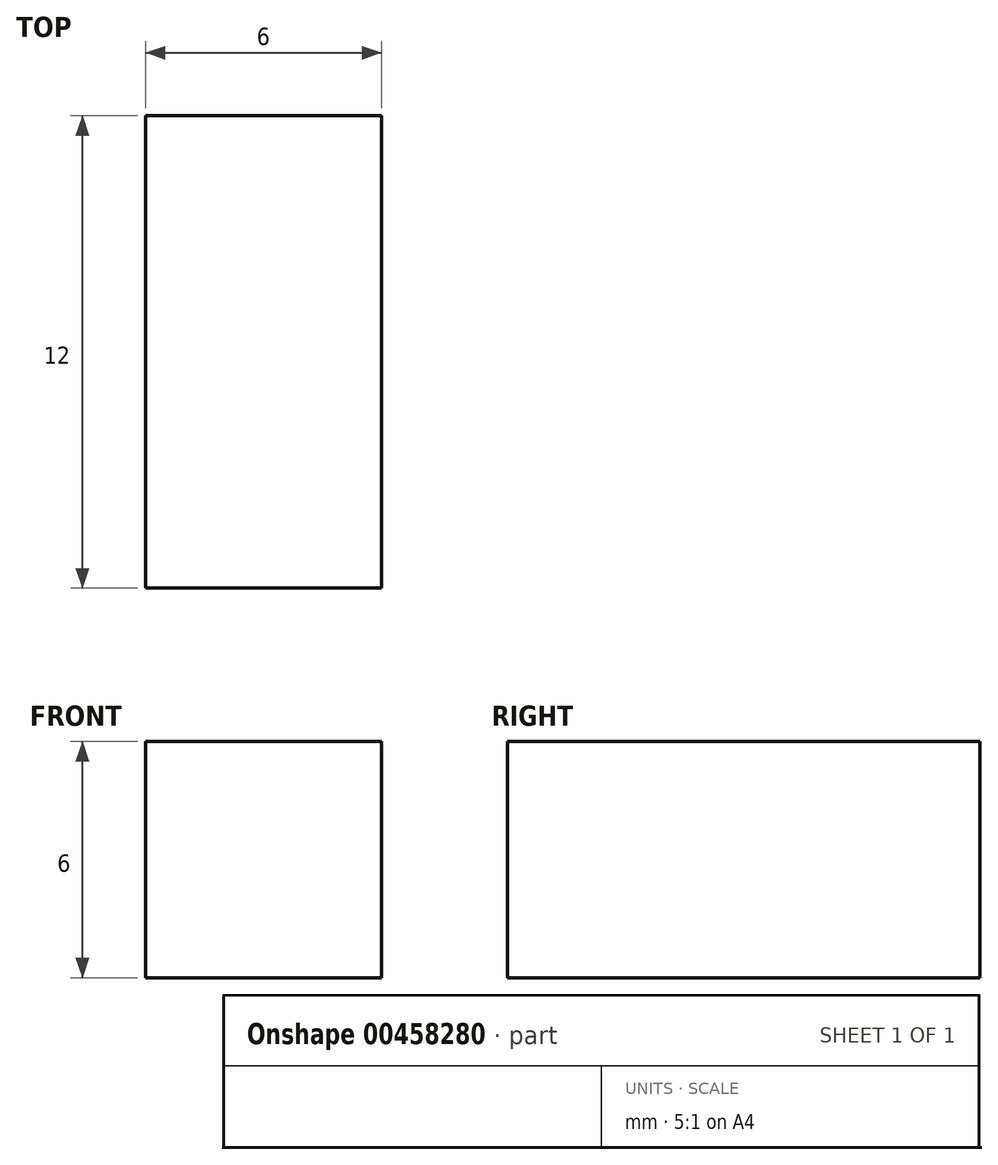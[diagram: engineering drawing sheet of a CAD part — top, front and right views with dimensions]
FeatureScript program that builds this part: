
annotation { "Feature Type Name" : "Feature", "Feature Type Description" : "" }
export const myFeature = defineFeature(function(context is Context, id is Id, definition is map)
    precondition{}
    {
        {
            var Q0;
            Q0=qCreatedBy(makeId("Front.planeOp"),FACE);
            var sketch = newSketch(context, id + "F0", { "sketchPlane" : qUnion([Q0])});
            skLineSegment(sketch, "E0.bottom", {"start": v(-3, 0) * mm, "end": v(3, 0) * mm});
            skLineSegment(sketch, "E0.top", {"start": v(-3, 6) * mm, "end": v(3, 6) * mm});
            skLineSegment(sketch, "E0.left", {"start": v(-3, 0) * mm, "end": v(-3, 6) * mm});
            skLineSegment(sketch, "E0.right", {"start": v(3, 0) * mm, "end": v(3, 6) * mm});
            skSolve(sketch);
        }
        {
            var Q0;
            Q0 = qSketchRegion(id + "F0", true);
            var Q1;
            Q1=makeQuery(id+"F0.imprint","IMPRINT",FACE,{"disambiguationData":[TD([[makeQuery(id+"F0.imprint","IMPRINT",EDGE,{"derivedFrom":sQuery(id+"F0.wireOp",EDGE,"E0.bottom")}),1.0]])]});
            extrude(context, id + "F1", {"entities" : qUnion([Q0, Q1]), "depth" : 12 * mm});
        }
    });
